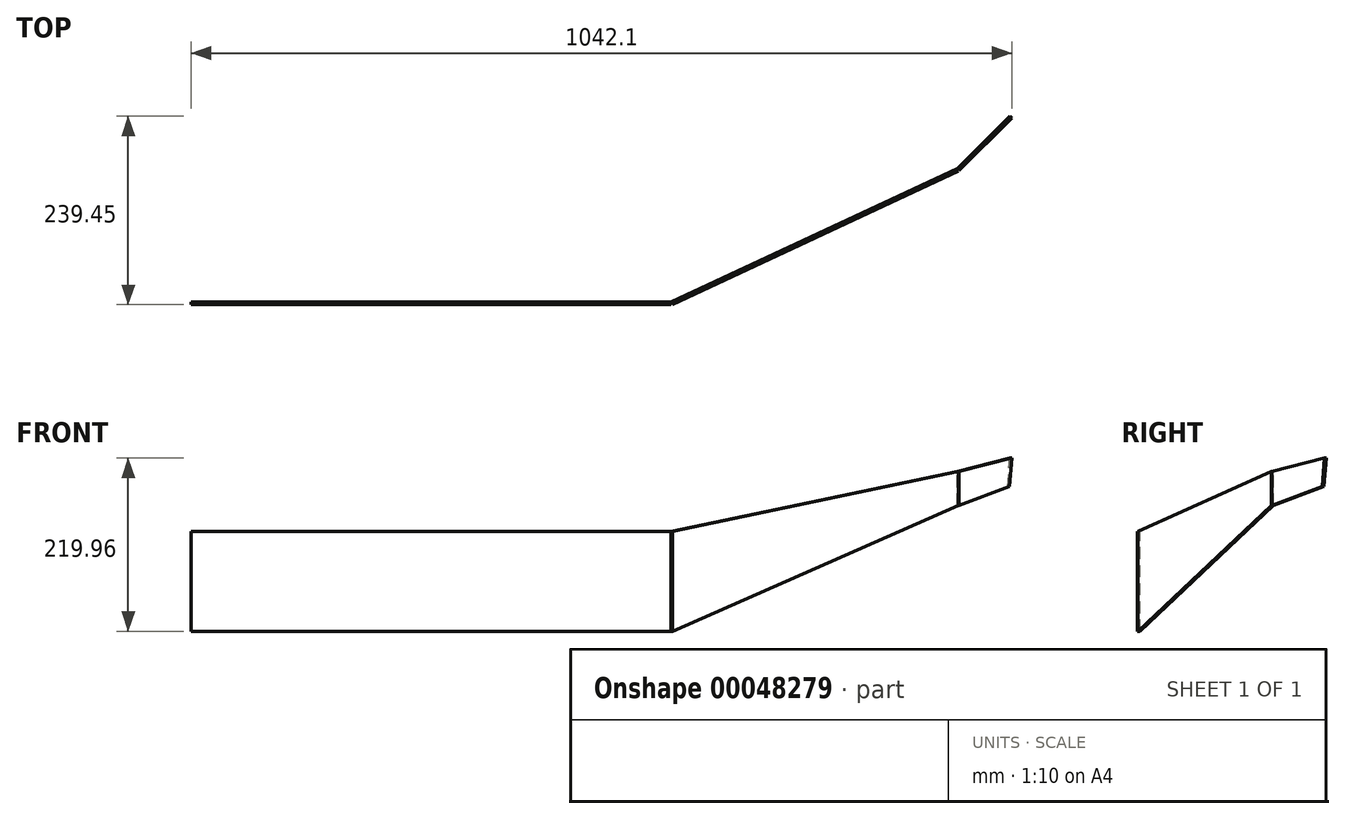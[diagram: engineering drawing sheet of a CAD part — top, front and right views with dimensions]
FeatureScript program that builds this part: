
annotation { "Feature Type Name" : "Feature", "Feature Type Description" : "" }
export const myFeature = defineFeature(function(context is Context, id is Id, definition is map)
    precondition{}
    {
        {
            var Q0;
            Q0=qCreatedBy(makeId("Front.planeOp"),FACE);
            var sketch = newSketch(context, id + "F0", { "sketchPlane" : qUnion([Q0])});
            skLineSegment(sketch, "E0.bottom", {"start": v(-304.8, -63.5) * mm, "end": v(304.8, -63.5) * mm});
            skLineSegment(sketch, "E0.top", {"start": v(-304.8, 63.5) * mm, "end": v(304.8, 63.5) * mm});
            skLineSegment(sketch, "E0.left", {"start": v(-304.8, -63.5) * mm, "end": v(-304.8, 63.5) * mm});
            skLineSegment(sketch, "E0.right", {"start": v(304.8, -63.5) * mm, "end": v(304.8, 63.5) * mm});
            skPoint(sketch, "E0.middle", {"position": v(0, 0) * mm});
            skSolve(sketch);
        }
        {
            var Q0;
            Q0 = qSketchRegion(id + "F0", true);
            extrude(context, id + "F1", {"entities" : qUnion([Q0]), "depth" : 3.17 * mm});
        }
        {
            var Q0;
            Q0=makeQuery(id+"F1.opExtrude","CAP_EDGE",EDGE,{"disambiguationData":[OSD([sQuery(id+"F0.wireOp",EDGE,"E0.right")])],"isStart":true});
            cPlane(context, id + "F2", {"entities" : qUnion([Q0]), "cplaneType" : CPlaneType.LINE_ANGLE, "offset" : 25.4 * mm, "angle" : 115 * degree, "width" : 152.4 * mm, "height" : 152.4 * mm});
        }
        {
            var Q0;
            Q0=qCreatedBy(id+"F2.planeOp",FACE);
            var sketch = newSketch(context, id + "F3", { "sketchPlane" : qUnion([Q0])});
            skLineSegment(sketch, "E1.0", {"start": v(-276.24, -63.5) * mm, "end": v(-276.24, 63.5) * mm});
            skLineSegment(sketch, "E2", {"start": v(-276.24, -63.5) * mm, "end": v(-677.28, 96.56) * mm});
            skLineSegment(sketch, "E3", {"start": v(-677.28, 96.56) * mm, "end": v(-677.28, 139.7) * mm});
            skLineSegment(sketch, "E4", {"start": v(-677.28, 139.7) * mm, "end": v(-276.24, 63.5) * mm});
            skSolve(sketch);
        }
        {
            var Q0;
            Q0 = qSketchRegion(id + "F3", true);
            extrude(context, id + "F4", {"entities" : qUnion([Q0]), "oppositeDirection" : true, "depth" : 3.17 * mm});
        }
        {
            var Q0;
            Q0=makeQuery(id+"F4.opExtrude","CAP_EDGE",EDGE,{"disambiguationData":[OSD([sQuery(id+"F3.wireOp",EDGE,"E3")])],"isStart":true});
            cPlane(context, id + "F5", {"entities" : qUnion([Q0]), "cplaneType" : CPlaneType.LINE_ANGLE, "offset" : 25.4 * mm, "angle" : 135 * degree, "width" : 152.4 * mm, "height" : 152.4 * mm});
        }
        {
            var Q0;
            Q0=qCreatedBy(id+"F5.planeOp",FACE);
            var sketch = newSketch(context, id + "F6", { "sketchPlane" : qUnion([Q0])});
            skLineSegment(sketch, "E5.0", {"start": v(-592.38, 96.56) * mm, "end": v(-592.38, 139.7) * mm});
            skLineSegment(sketch, "E6", {"start": v(-592.38, 96.56) * mm, "end": v(-683.17, 120.82) * mm});
            skLineSegment(sketch, "E7", {"start": v(-683.17, 120.82) * mm, "end": v(-686.84, 156.46) * mm});
            skLineSegment(sketch, "E8", {"start": v(-686.84, 156.46) * mm, "end": v(-592.38, 139.7) * mm});
            skSolve(sketch);
        }
        {
            var Q0;
            Q0 = qSketchRegion(id + "F6", true);
            extrude(context, id + "F7", {"entities" : qUnion([Q0]), "oppositeDirection" : true, "depth" : 3.17 * mm});
        }
    });
